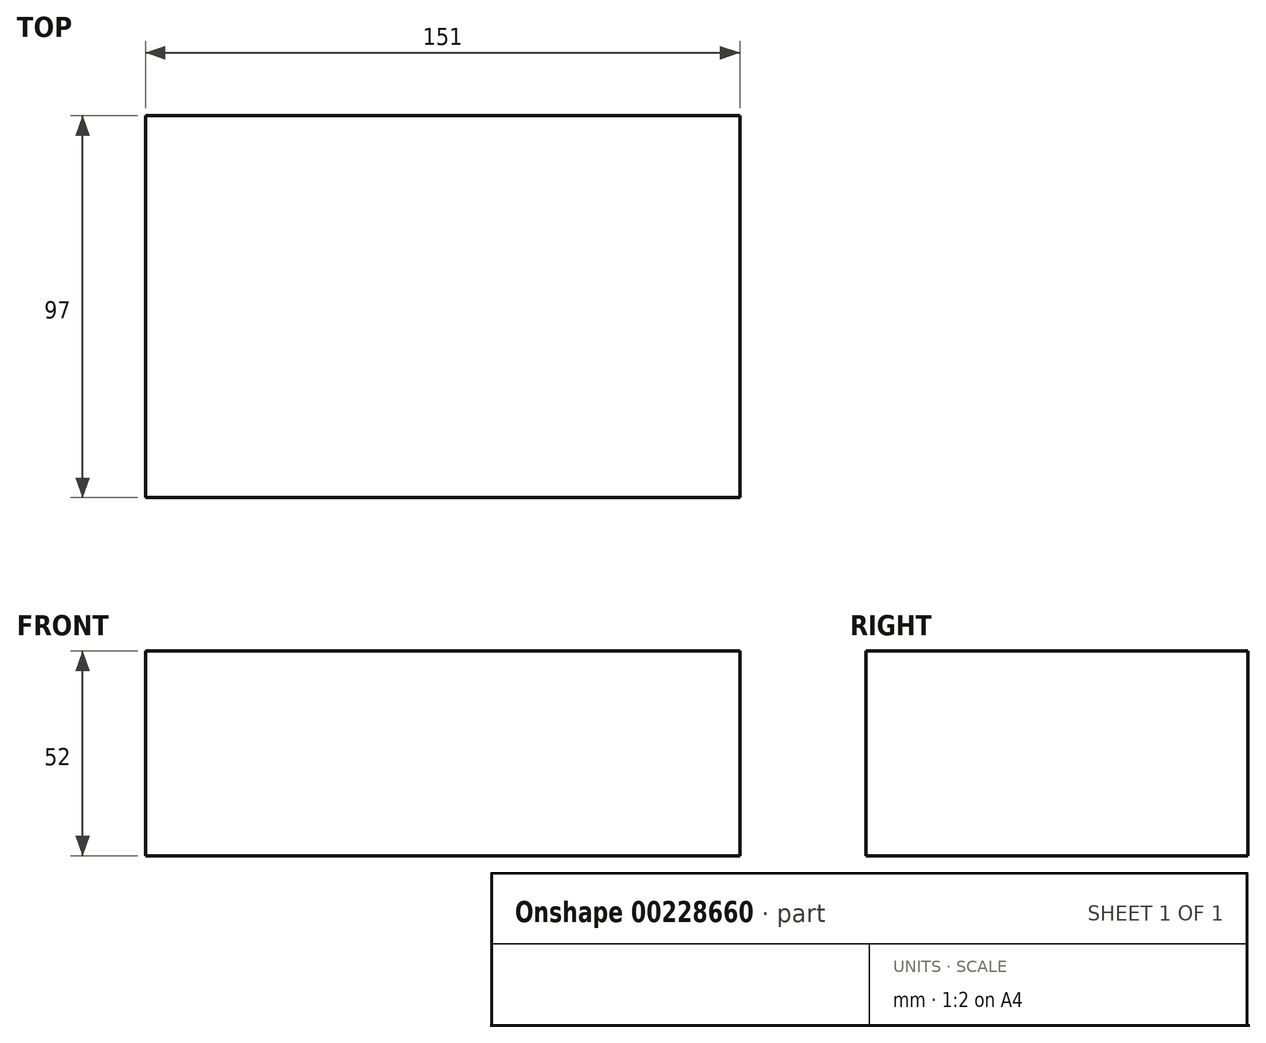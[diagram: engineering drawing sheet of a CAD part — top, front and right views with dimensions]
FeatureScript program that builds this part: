
annotation { "Feature Type Name" : "Feature", "Feature Type Description" : "" }
export const myFeature = defineFeature(function(context is Context, id is Id, definition is map)
    precondition{}
    {
        {
            var Q0;
            Q0=qCreatedBy(makeId("Top.planeOp"),FACE);
            var sketch = newSketch(context, id + "F0", { "sketchPlane" : qUnion([Q0])});
            skLineSegment(sketch, "E0.bottom", {"start": v(75.5, -48.5) * mm, "end": v(-75.5, -48.5) * mm});
            skLineSegment(sketch, "E0.top", {"start": v(75.5, 48.5) * mm, "end": v(-75.5, 48.5) * mm});
            skLineSegment(sketch, "E0.left", {"start": v(75.5, -48.5) * mm, "end": v(75.5, 48.5) * mm});
            skLineSegment(sketch, "E0.right", {"start": v(-75.5, -48.5) * mm, "end": v(-75.5, 48.5) * mm});
            skPoint(sketch, "E0.middle", {"position": v(0, 0) * mm});
            skSolve(sketch);
        }
        {
            var Q0;
            Q0 = qSketchRegion(id + "F0", true);
            extrude(context, id + "F1", {"entities" : qUnion([Q0]), "depth" : 52 * mm});
        }
    });
